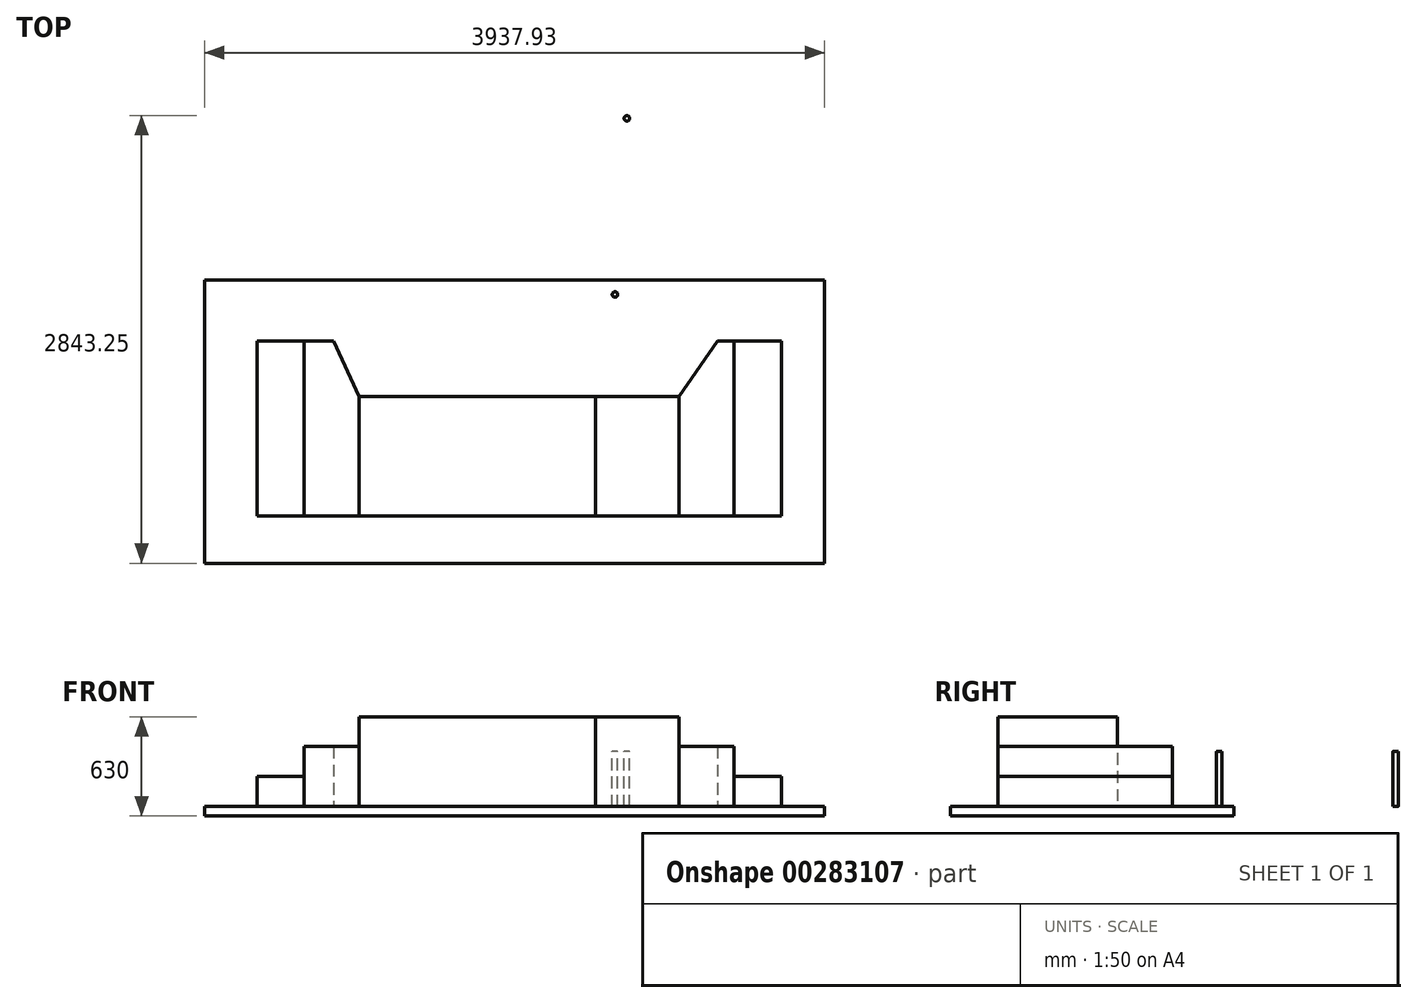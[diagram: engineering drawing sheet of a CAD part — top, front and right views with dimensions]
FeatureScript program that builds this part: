
annotation { "Feature Type Name" : "Feature", "Feature Type Description" : "" }
export const myFeature = defineFeature(function(context is Context, id is Id, definition is map)
    precondition{}
    {
        {
            var Q0;
            Q0=qCreatedBy(makeId("Top.planeOp"),FACE);
            var sketch = newSketch(context, id + "F0", { "sketchPlane" : qUnion([Q0])});
            skLineSegment(sketch, "E0.bottom", {"start": v(0, 0) * mm, "end": v(-1500, 0) * mm});
            skLineSegment(sketch, "E0.top", {"start": v(0, 760) * mm, "end": v(-1500, 760) * mm});
            skLineSegment(sketch, "E0.left", {"start": v(0, 0) * mm, "end": v(0, 760) * mm});
            skLineSegment(sketch, "E0.right", {"start": v(-1500, 0) * mm, "end": v(-1500, 760) * mm});
            skLineSegment(sketch, "E1.bottom", {"start": v(0, 760) * mm, "end": v(530, 760) * mm});
            skLineSegment(sketch, "E1.top", {"start": v(0, 0) * mm, "end": v(530, 0) * mm});
            skLineSegment(sketch, "E1.left", {"start": v(0, 760) * mm, "end": v(0, 0) * mm});
            skLineSegment(sketch, "E1.right", {"start": v(530, 760) * mm, "end": v(530, 0) * mm});
            skLineSegment(sketch, "E2", {"start": v(-1500, 0) * mm, "end": v(-1850, 0) * mm});
            skLineSegment(sketch, "E3", {"start": v(-1850, 0) * mm, "end": v(-1850, 1110) * mm});
            skLineSegment(sketch, "E4", {"start": v(-1663.2, 1110) * mm, "end": v(-1500, 760) * mm});
            skLineSegment(sketch, "E5.bottom", {"start": v(-1850, 0) * mm, "end": v(-2150, 0) * mm});
            skLineSegment(sketch, "E5.top", {"start": v(-1850, 1110) * mm, "end": v(-2150, 1110) * mm});
            skLineSegment(sketch, "E5.right", {"start": v(-2150, 0) * mm, "end": v(-2150, 1110) * mm});
            skLineSegment(sketch, "E6", {"start": v(530, 0) * mm, "end": v(880, 0) * mm});
            skLineSegment(sketch, "E7", {"start": v(880, 0) * mm, "end": v(880, 1110) * mm});
            skLineSegment(sketch, "E8", {"start": v(775.07, 1110) * mm, "end": v(530, 760) * mm});
            skLineSegment(sketch, "E9.bottom", {"start": v(880, 0) * mm, "end": v(1180, 0) * mm});
            skLineSegment(sketch, "E9.top", {"start": v(880, 1110) * mm, "end": v(1180, 1110) * mm});
            skLineSegment(sketch, "E9.right", {"start": v(1180, 0) * mm, "end": v(1180, 1110) * mm});
            skLineSegment(sketch, "E10", {"start": v(-1850, 1110) * mm, "end": v(-1663.2, 1110) * mm});
            skLineSegment(sketch, "E11", {"start": v(880, 1110) * mm, "end": v(775.07, 1110) * mm});
            skSolve(sketch);
        }
        {
            var Q0;
            Q0=makeQuery(id+"F0.imprint","IMPRINT",FACE,{"disambiguationData":[TD([[makeQuery(id+"F0.imprint","IMPRINT",EDGE,{"derivedFrom":sQuery(id+"F0.wireOp",EDGE,"E5.bottom")}),-1.0]])]});
            var Q1;
            Q1=makeQuery(id+"F0.imprint","IMPRINT",FACE,{"disambiguationData":[TD([[makeQuery(id+"F0.imprint","IMPRINT",EDGE,{"derivedFrom":sQuery(id+"F0.wireOp",EDGE,"E9.bottom")}),1.0]])]});
            extrude(context, id + "F1", {"entities" : qUnion([Q0, Q1]), "depth" : 190 * mm});
        }
        {
            var Q0;
            Q0=makeQuery(id+"F0.imprint","IMPRINT",FACE,{"disambiguationData":[TD([[makeQuery(id+"F0.imprint","IMPRINT",EDGE,{"derivedFrom":sQuery(id+"F0.wireOp",EDGE,"E0.right")}),1.0]])]});
            var Q1;
            Q1=makeQuery(id+"F0.imprint","IMPRINT",FACE,{"disambiguationData":[TD([[makeQuery(id+"F0.imprint","IMPRINT",EDGE,{"derivedFrom":sQuery(id+"F0.wireOp",EDGE,"E1.right")}),1.0]])]});
            extrude(context, id + "F2", {"entities" : qUnion([Q0, Q1]), "depth" : 380 * mm});
        }
        {
            var Q0;
            Q0=makeQuery(id+"F0.imprint","IMPRINT",FACE,{"disambiguationData":[TD([[makeQuery(id+"F0.imprint","IMPRINT",EDGE,{"derivedFrom":sQuery(id+"F0.wireOp",EDGE,"E0.bottom")}),-1.0]])]});
            extrude(context, id + "F3", {"entities" : qUnion([Q0]), "depth" : 570 * mm});
        }
        {
            var Q0;
            Q0=makeQuery(id+"F0.imprint","IMPRINT",FACE,{"disambiguationData":[TD([[makeQuery(id+"F0.imprint","IMPRINT",EDGE,{"derivedFrom":sQuery(id+"F0.wireOp",EDGE,"E1.bottom")}),-1.0]])]});
            var Q1;
            Q1=makeQuery(id+"F3.opExtrude","CAP_FACE",FACE,{"disambiguationData":[OSD([sQuery(id+"F0.wireOp",EDGE,"E0.bottom"),sQuery(id+"F0.wireOp",EDGE,"E0.top"),sQuery(id+"F0.wireOp",EDGE,"E0.right"),sQuery(id+"F0.wireOp",EDGE,"E1.left")])],"isStart":false});
            extrude(context, id + "F4", {"entities" : qUnion([Q0]), "endBound" : BoundingType.UP_TO_SURFACE, "endBoundEntityFace" : qUnion([Q1]), "depth" : 25 * mm});
        }
        {
            var Q0;
            Q0=makeQuery(id+"F3.opExtrude","SWEPT_FACE",FACE,{"disambiguationData":[OSD([sQuery(id+"F0.wireOp",EDGE,"E0.bottom")])]});
            var sketch = newSketch(context, id + "F5", { "sketchPlane" : qUnion([Q0])});
            skLineSegment(sketch, "E12.bottom", {"start": v(1454.75, 0) * mm, "end": v(-2483.18, 0) * mm});
            skLineSegment(sketch, "E12.top", {"start": v(1454.75, -60) * mm, "end": v(-2483.18, -60) * mm});
            skLineSegment(sketch, "E12.left", {"start": v(1454.75, 0) * mm, "end": v(1454.75, -60) * mm});
            skLineSegment(sketch, "E12.right", {"start": v(-2483.18, 0) * mm, "end": v(-2483.18, -60) * mm});
            skSolve(sketch);
        }
        {
            var Q0;
            Q0=makeQuery(id+"F5.imprint","IMPRINT",FACE,{"disambiguationData":[TD([[makeQuery(id+"F5.imprint","IMPRINT",EDGE,{"derivedFrom":sQuery(id+"F5.wireOp",EDGE,"E12.top")}),-1.0]])]});
            extrude(context, id + "F6", {"entities" : qUnion([Q0]), "depth" : 300 * mm, "hasSecondDirection" : true, "secondDirectionOppositeDirection" : true, "secondDirectionDepth" : 1500 * mm});
        }
        {
            var Q0;
            Q0=qCreatedBy(makeId("Top.planeOp"),FACE);
            var sketch = newSketch(context, id + "F7", { "sketchPlane" : qUnion([Q0])});
            skLineSegment(sketch, "E13.bottom", {"start": v(273.97, 1309.25) * mm, "end": v(-1076.03, 1309.25) * mm});
            skLineSegment(sketch, "E13.top", {"start": v(273.97, 2613.25) * mm, "end": v(-1076.03, 2613.25) * mm});
            skLineSegment(sketch, "E13.left", {"start": v(273.97, 1309.25) * mm, "end": v(273.97, 2613.25) * mm});
            skLineSegment(sketch, "E13.right", {"start": v(-1076.03, 1309.25) * mm, "end": v(-1076.03, 2613.25) * mm});
            skSolve(sketch);
        }
        {
            var Q0;
            Q0=makeQuery(id+"F7.imprint","IMPRINT",FACE,{"disambiguationData":[TD([[makeQuery(id+"F7.imprint","IMPRINT",EDGE,{"derivedFrom":sQuery(id+"F7.wireOp",EDGE,"E13.bottom")}),-1.0]])]});
            extrude(context, id + "F8", {"entities" : qUnion([Q0]), "depth" : (54 + 235.5) * mm});
        }
        {
            var Q0;
            Q0=makeQuery(id+"F8.opExtrude","CAP_FACE",FACE,{"disambiguationData":[OSD([sQuery(id+"F7.wireOp",EDGE,"E13.bottom"),sQuery(id+"F7.wireOp",EDGE,"E13.top"),sQuery(id+"F7.wireOp",EDGE,"E13.left"),sQuery(id+"F7.wireOp",EDGE,"E13.right")])],"isStart":false});
            var sketch = newSketch(context, id + "F9", { "sketchPlane" : qUnion([Q0])});
            skLineSegment(sketch, "E14.bottom", {"start": v(-1076.03, 2613.25) * mm, "end": v(273.97, 2613.25) * mm});
            skLineSegment(sketch, "E14.top", {"start": v(-1076.03, 963.25) * mm, "end": v(273.97, 963.25) * mm});
            skLineSegment(sketch, "E14.left", {"start": v(-1076.03, 2613.25) * mm, "end": v(-1076.03, 963.25) * mm});
            skLineSegment(sketch, "E14.right", {"start": v(273.97, 2613.25) * mm, "end": v(273.97, 963.25) * mm});
            skSolve(sketch);
        }
        {
            var Q0;
            {var subQ0=sQuery(id+"F9.wireOp",EDGE,"E14.top");Q0=makeQuery(id+"F9.imprint","IMPRINT",FACE,{"disambiguationData":[TD([[makeQuery(id+"F9.imprint","IMPRINT",EDGE,{"derivedFrom":subQ0}),1.0]])]});}
            var Q1;
            {var subQ0=sQuery(id+"F9.wireOp",EDGE,"E14.bottom");Q1=makeQuery(id+"F9.imprint","IMPRINT",FACE,{"disambiguationData":[TD([[makeQuery(id+"F9.imprint","IMPRINT",EDGE,{"derivedFrom":subQ0}),1.0]])]});}
            extrude(context, id + "F10", {"entities" : qUnion([Q0, Q1]), "operationType" : NewBodyOperationType.ADD, "depth" : 60.18 * mm});
        }
        {
            var Q0;
            Q0=makeQuery(id+"F10.opExtrude","CAP_FACE",FACE,{"disambiguationData":[OSD([sQuery(id+"F9.wireOp",EDGE,"E14.bottom"),sQuery(id+"F9.wireOp",EDGE,"E14.top"),sQuery(id+"F9.wireOp",EDGE,"E14.left"),sQuery(id+"F9.wireOp",EDGE,"E14.right")])],"isStart":false});
            var sketch = newSketch(context, id + "F11", { "sketchPlane" : qUnion([Q0])});
            skLineSegment(sketch, "E15", {"start": v(-1076.03, 1406.75) * mm, "end": v(273.97, 1406.75) * mm, "construction": true});
            skLineSegment(sketch, "E16", {"start": v(-1076.03, 2525.75) * mm, "end": v(273.97, 2525.75) * mm, "construction": true});
            skCircle(sketch, "E17", {"center": v(-926.03, 1406.75) * mm, "radius": 17.5 * mm});
            skCircle(sketch, "E18", {"center": v(-1002.03, 2525.75) * mm, "radius": 17.5 * mm});
            skLineSegment(sketch, "E19", {"start": v(-401.03, 963.25) * mm, "end": v(-401.03, 2613.25) * mm, "construction": true});
            skCircle(sketch, "E20.MirrorC", {"center": v(123.97, 1406.75) * mm, "radius": 17.5 * mm});
            skCircle(sketch, "E21.MirrorC", {"center": v(199.97, 2525.75) * mm, "radius": 17.5 * mm});
            skSolve(sketch);
        }
        {
            var Q0;
            Q0=makeQuery(id+"F11.imprint","IMPRINT",FACE,{"disambiguationData":[TD([[makeQuery(id+"F11.imprint","IMPRINT",EDGE,{"derivedFrom":sQuery(id+"F11.wireOp",EDGE,"E21.MirrorC")}),-1.0]])]});
            var Q1;
            Q1=makeQuery(id+"F11.imprint","IMPRINT",FACE,{"disambiguationData":[TD([[makeQuery(id+"F11.imprint","IMPRINT",EDGE,{"derivedFrom":sQuery(id+"F11.wireOp",EDGE,"E20.MirrorC")}),-1.0]])]});
            var Q2;
            Q2=makeQuery(id+"F11.imprint","IMPRINT",FACE,{"disambiguationData":[TD([[makeQuery(id+"F11.imprint","IMPRINT",EDGE,{"derivedFrom":sQuery(id+"F11.wireOp",EDGE,"E17")}),1.0]])]});
            var Q3;
            Q3=makeQuery(id+"F11.imprint","IMPRINT",FACE,{"disambiguationData":[TD([[makeQuery(id+"F11.imprint","IMPRINT",EDGE,{"derivedFrom":sQuery(id+"F11.wireOp",EDGE,"E18")}),1.0]])]});
            var Q4;
            Q4=makeQuery(id+"F8.opExtrude","CAP_FACE",FACE,{"disambiguationData":[OSD([sQuery(id+"F7.wireOp",EDGE,"E13.bottom"),sQuery(id+"F7.wireOp",EDGE,"E13.top"),sQuery(id+"F7.wireOp",EDGE,"E13.left"),sQuery(id+"F7.wireOp",EDGE,"E13.right")])],"isStart":true});
            extrude(context, id + "F12", {"entities" : qUnion([Q0, Q1, Q2, Q3]), "operationType" : NewBodyOperationType.REMOVE, "endBound" : BoundingType.UP_TO_SURFACE, "oppositeDirection" : true, "endBoundEntityFace" : qUnion([Q4]), "depth" : 25 * mm});
        }
    });
